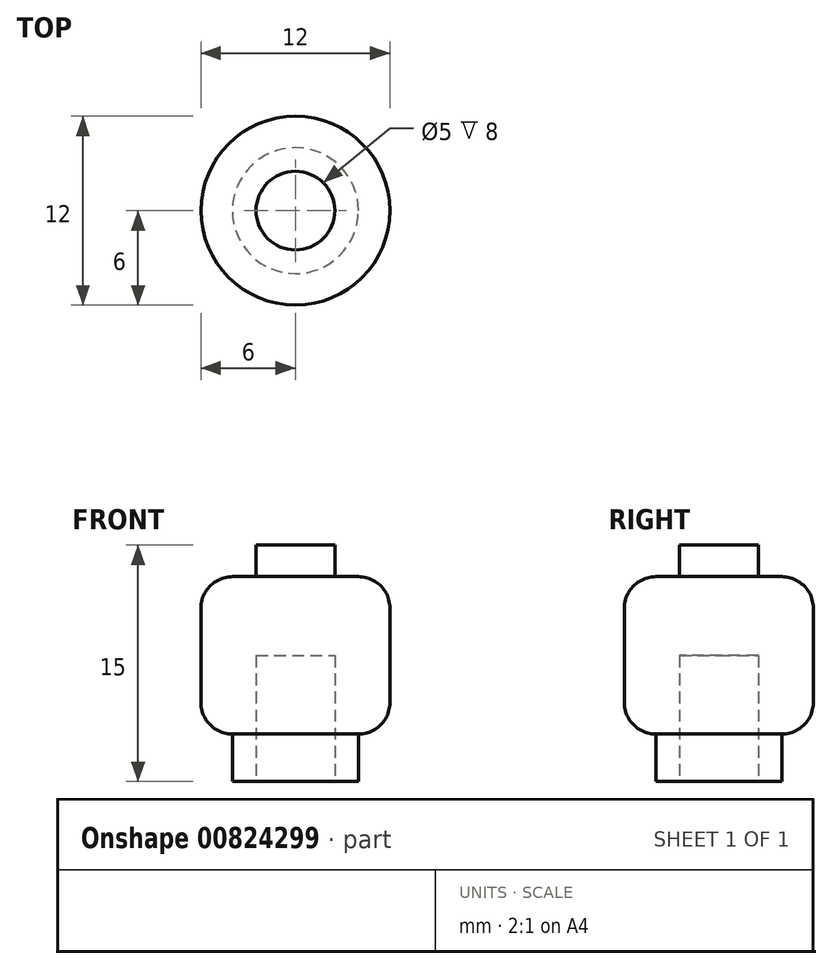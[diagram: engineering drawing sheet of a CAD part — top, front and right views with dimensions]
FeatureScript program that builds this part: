
annotation { "Feature Type Name" : "Feature", "Feature Type Description" : "" }
export const myFeature = defineFeature(function(context is Context, id is Id, definition is map)
    precondition{}
    {
        {
            var Q0;
            Q0=qCreatedBy(makeId("Top.planeOp"),FACE);
            var sketch = newSketch(context, id + "F0", { "sketchPlane" : qUnion([Q0])});
            skCircle(sketch, "E0", {"center": v(0, 0) * mm, "radius": 4 * mm});
            skSolve(sketch);
        }
        {
            var Q0;
            Q0 = qSketchRegion(id + "F0", true);
            extrude(context, id + "F1", {"entities" : qUnion([Q0]), "depth" : 3 * mm, "offsetDistance" : 25 * mm});
        }
        {
            var Q0;
            Q0=makeQuery(id+"F1.opExtrude","CAP_FACE",FACE,{"disambiguationData":[OSD([sQuery(id+"F0.wireOp",EDGE,"E0")])],"isStart":false});
            var sketch = newSketch(context, id + "F2", { "sketchPlane" : qUnion([Q0])});
            skCircle(sketch, "E1", {"center": v(0, 0) * mm, "radius": 6 * mm});
            skSolve(sketch);
        }
        {
            var Q0;
            Q0 = qSketchRegion(id + "F2", true);
            extrude(context, id + "F3", {"entities" : qUnion([Q0]), "operationType" : NewBodyOperationType.ADD, "depth" : 10 * mm, "offsetDistance" : 25 * mm});
        }
        {
            var Q0;
            Q0 = qSketchRegion(id + "F2", true);
            extrude(context, id + "F4", {"entities" : qUnion([Q0]), "operationType" : NewBodyOperationType.ADD, "depth" : 8 * mm, "offsetDistance" : 25 * mm});
        }
        {
            var Q0;
            Q0=makeQuery(id+"F3.opExtrude","CAP_FACE",FACE,{"disambiguationData":[OSD([sQuery(id+"F2.wireOp",EDGE,"E1")])],"isStart":false});
            var sketch = newSketch(context, id + "F5", { "sketchPlane" : qUnion([Q0])});
            skCircle(sketch, "E2", {"center": v(0, 0) * mm, "radius": 2.5 * mm});
            skSolve(sketch);
        }
        {
            var Q0;
            Q0 = qSketchRegion(id + "F5", true);
            extrude(context, id + "F6", {"entities" : qUnion([Q0]), "operationType" : NewBodyOperationType.ADD, "depth" : 2 * mm, "offsetDistance" : 25 * mm});
        }
        {
            var Q0;
            Q0=makeQuery(id+"F3.opExtrude","CAP_EDGE",EDGE,{"disambiguationData":[OSD([sQuery(id+"F2.wireOp",EDGE,"E1")])],"isStart":false});
            var Q1;
            Q1=makeQuery(id+"F3.opExtrude","CAP_EDGE",EDGE,{"disambiguationData":[OSD([sQuery(id+"F2.wireOp",EDGE,"E1")])],"isStart":true});
            fillet(context, id + "F7", {"entities" : qUnion([Q0, Q1]), "radius" : 2 * mm, "tangentPropagation" : true, "allowEdgeOverflow" : false});
        }
        {
            var Q0;
            Q0=makeQuery(id+"F1.opExtrude","CAP_FACE",FACE,{"disambiguationData":[OSD([sQuery(id+"F0.wireOp",EDGE,"E0")])],"isStart":true});
            var sketch = newSketch(context, id + "F8", { "sketchPlane" : qUnion([Q0])});
            skCircle(sketch, "E3", {"center": v(0, 0) * mm, "radius": 2.5 * mm});
            skSolve(sketch);
        }
        {
            var Q0;
            Q0 = qSketchRegion(id + "F8", true);
            extrude(context, id + "F9", {"entities" : qUnion([Q0]), "operationType" : NewBodyOperationType.REMOVE, "oppositeDirection" : true, "depth" : 8 * mm, "offsetDistance" : 25 * mm});
        }
    });
